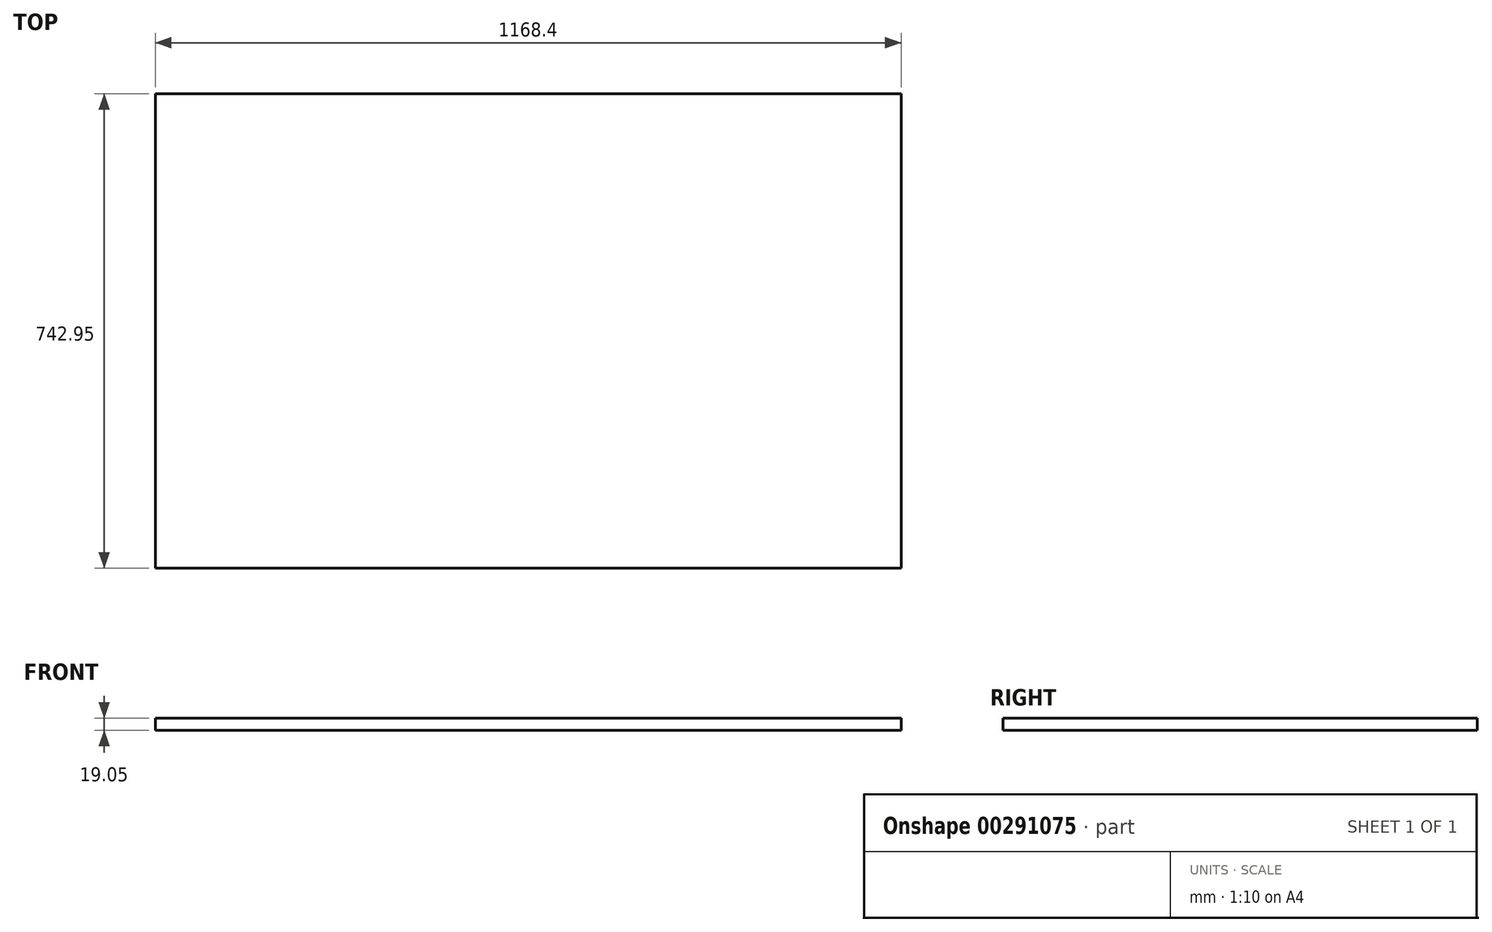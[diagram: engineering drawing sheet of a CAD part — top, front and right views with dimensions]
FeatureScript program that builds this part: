
annotation { "Feature Type Name" : "Feature", "Feature Type Description" : "" }
export const myFeature = defineFeature(function(context is Context, id is Id, definition is map)
    precondition{}
    {
        {
            var Q0;
            Q0=qCreatedBy(makeId("Top.planeOp"),FACE);
            var sketch = newSketch(context, id + "F0", { "sketchPlane" : qUnion([Q0])});
            skLineSegment(sketch, "E0.bottom", {"start": v(0, 0) * mm, "end": v(1168.4, 0) * mm});
            skLineSegment(sketch, "E0.top", {"start": v(0, -742.95) * mm, "end": v(1168.4, -742.95) * mm});
            skLineSegment(sketch, "E0.left", {"start": v(0, 0) * mm, "end": v(0, -742.95) * mm});
            skLineSegment(sketch, "E0.right", {"start": v(1168.4, 0) * mm, "end": v(1168.4, -742.95) * mm});
            skSolve(sketch);
        }
        {
            var Q0;
            Q0 = qSketchRegion(id + "F0", true);
            extrude(context, id + "F1", {"entities" : qUnion([Q0]), "oppositeDirection" : true, "depth" : 19.05 * mm});
        }
    });
